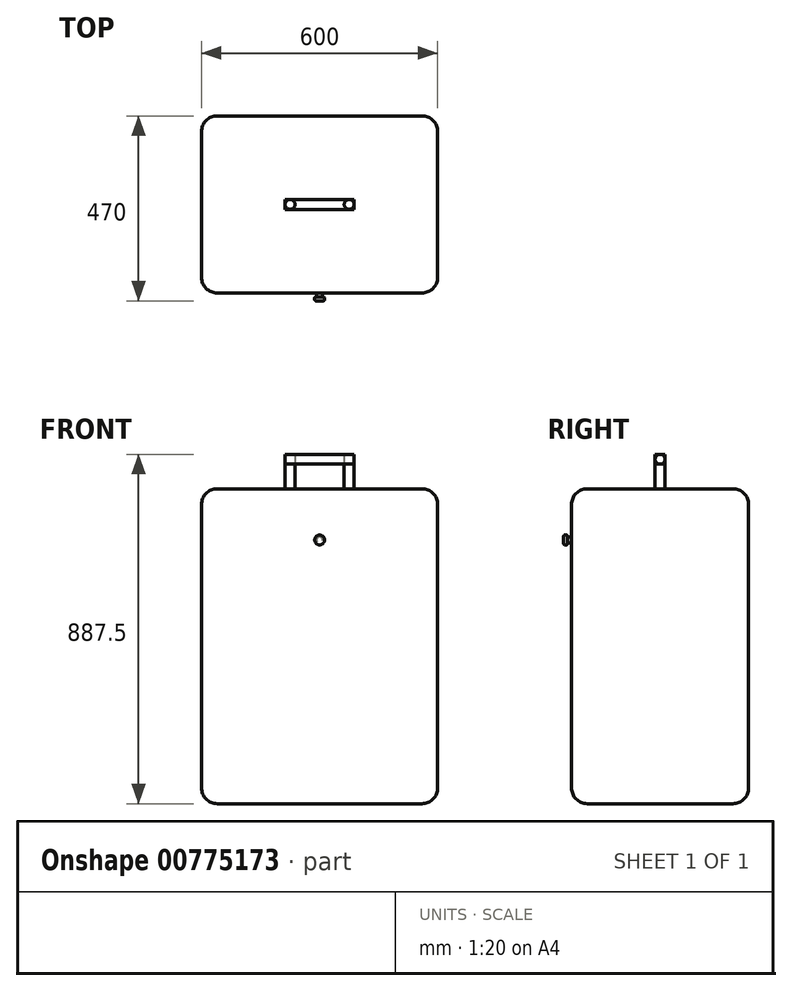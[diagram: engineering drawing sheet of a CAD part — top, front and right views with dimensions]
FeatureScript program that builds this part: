
annotation { "Feature Type Name" : "Feature", "Feature Type Description" : "" }
export const myFeature = defineFeature(function(context is Context, id is Id, definition is map)
    precondition{}
    {
        {
            var Q0;
            Q0=qCreatedBy(makeId("Top.planeOp"),FACE);
            var sketch = newSketch(context, id + "F0", { "sketchPlane" : qUnion([Q0])});
            skLineSegment(sketch, "E0.bottom", {"start": v(300, -225) * mm, "end": v(-300, -225) * mm});
            skLineSegment(sketch, "E0.top", {"start": v(300, 225) * mm, "end": v(-300, 225) * mm});
            skLineSegment(sketch, "E0.left", {"start": v(300, -225) * mm, "end": v(300, 225) * mm});
            skLineSegment(sketch, "E0.right", {"start": v(-300, -225) * mm, "end": v(-300, 225) * mm});
            skPoint(sketch, "E0.middle", {"position": v(0, 0) * mm});
            skSolve(sketch);
        }
        {
            var Q0;
            Q0 = qSketchRegion(id + "F0", true);
            extrude(context, id + "F1", {"entities" : qUnion([Q0]), "depth" : 800 * mm, "offsetDistance" : 25 * mm});
        }
        {
            var Q0;
            Q0=makeQuery(id+"F1.opExtrude","SWEPT_FACE",FACE,{"disambiguationData":[OSD([sQuery(id+"F0.wireOp",EDGE,"E0.bottom")])]});
            var Q1;
            Q1=makeQuery(id+"F1.opExtrude","CAP_FACE",FACE,{"disambiguationData":[OSD([sQuery(id+"F0.wireOp",EDGE,"E0.bottom"),sQuery(id+"F0.wireOp",EDGE,"E0.top"),sQuery(id+"F0.wireOp",EDGE,"E0.left"),sQuery(id+"F0.wireOp",EDGE,"E0.right")])],"isStart":false});
            var Q2;
            Q2=makeQuery(id+"F1.opExtrude","SWEPT_FACE",FACE,{"disambiguationData":[OSD([sQuery(id+"F0.wireOp",EDGE,"E0.top")])]});
            var Q3;
            Q3=makeQuery(id+"F1.opExtrude","CAP_FACE",FACE,{"disambiguationData":[OSD([sQuery(id+"F0.wireOp",EDGE,"E0.bottom"),sQuery(id+"F0.wireOp",EDGE,"E0.top"),sQuery(id+"F0.wireOp",EDGE,"E0.left"),sQuery(id+"F0.wireOp",EDGE,"E0.right")])],"isStart":true});
            fillet(context, id + "F2", {"entities" : qUnion([Q0, Q1, Q2, Q3]), "radius" : 40 * mm, "tangentPropagation" : true, "allowEdgeOverflow" : false});
        }
        {
            var Q0;
            Q0=makeQuery(id+"F1.opExtrude","CAP_FACE",FACE,{"disambiguationData":[OSD([sQuery(id+"F0.wireOp",EDGE,"E0.bottom"),sQuery(id+"F0.wireOp",EDGE,"E0.top"),sQuery(id+"F0.wireOp",EDGE,"E0.left"),sQuery(id+"F0.wireOp",EDGE,"E0.right")])],"isStart":false});
            var sketch = newSketch(context, id + "F3", { "sketchPlane" : qUnion([Q0])});
            skLineSegment(sketch, "E1", {"start": v(0, 185) * mm, "end": v(0, -185) * mm});
            skCircle(sketch, "E2", {"center": v(-75, 0) * mm, "radius": 12.5 * mm});
            skCircle(sketch, "E3.MirrorC", {"center": v(75, 0) * mm, "radius": 12.5 * mm});
            skSolve(sketch);
        }
        {
            var Q0;
            Q0 = qSketchRegion(id + "F3", true);
            extrude(context, id + "F4", {"entities" : qUnion([Q0]), "operationType" : NewBodyOperationType.ADD, "depth" : 75 * mm, "offsetDistance" : 25 * mm});
        }
        {
            var Q0;
            Q0=makeQuery(id+"F4.opExtrude","CAP_FACE",FACE,{"disambiguationData":[OSD([sQuery(id+"F3.wireOp",EDGE,"E2")])],"isStart":false});
            var sketch = newSketch(context, id + "F5", { "sketchPlane" : qUnion([Q0])});
            skLineSegment(sketch, "E4", {"start": v(-75, 0) * mm, "end": v(74.49, 0) * mm});
            skSolve(sketch);
        }
        {
            var Q0;
            Q0=qCreatedBy(makeId("Right.planeOp"),FACE);
            var sketch = newSketch(context, id + "F6", { "sketchPlane" : qUnion([Q0])});
            skCircle(sketch, "E5", {"center": v(0, 875) * mm, "radius": 12.5 * mm});
            skSolve(sketch);
        }
        {
            var Q0;
            Q0=makeQuery(id+"F5.imprint","IMPRINT",FACE,{"disambiguationData":[TD([[makeQuery(id+"F5.imprint","IMPRINT",EDGE,{"derivedFrom":makeQuery(id+"F4.opExtrude","CAP_EDGE",EDGE,{"disambiguationData":[OSD([sQuery(id+"F3.wireOp",EDGE,"E2")])],"isStart":false})}),1.0]])]});
            extrude(context, id + "F7", {"entities" : qUnion([Q0]), "operationType" : NewBodyOperationType.ADD, "oppositeDirection" : true, "depth" : 12.5 * mm, "offsetDistance" : 25 * mm});
        }
        {
            var Q0;
            Q0=makeQuery(id+"F4.opExtrude","CAP_FACE",FACE,{"disambiguationData":[OSD([sQuery(id+"F3.wireOp",EDGE,"E2")])],"isStart":false});
            extrude(context, id + "F8", {"entities" : qUnion([Q0]), "operationType" : NewBodyOperationType.ADD, "oppositeDirection" : true, "depth" : 12.5 * mm, "offsetDistance" : 25 * mm});
        }
        {
            var Q0;
            Q0=makeQuery(id+"F4.opExtrude","CAP_FACE",FACE,{"disambiguationData":[OSD([sQuery(id+"F3.wireOp",EDGE,"E2")])],"isStart":false});
            extrude(context, id + "F9", {"entities" : qUnion([Q0]), "operationType" : NewBodyOperationType.REMOVE, "oppositeDirection" : true, "depth" : 12.5 * mm, "offsetDistance" : 25 * mm});
        }
        {
            var Q0;
            Q0 = qSketchRegion(id + "F6", true);
            extrude(context, id + "F10", {"entities" : qUnion([Q0]), "oppositeDirection" : true, "depth" : 62.5 * mm, "offsetDistance" : 25 * mm});
        }
        {
            var Q0;
            Q0=makeQuery(id+"F10.opExtrude","CAP_FACE",FACE,{"disambiguationData":[OSD([sQuery(id+"F6.wireOp",EDGE,"E5")])],"isStart":true});
            extrude(context, id + "F11", {"entities" : qUnion([Q0]), "operationType" : NewBodyOperationType.ADD, "depth" : 62.5 * mm, "offsetDistance" : 25 * mm});
        }
        {
            var Q0;
            Q0=makeQuery(id+"F4.opExtrude","CAP_FACE",FACE,{"disambiguationData":[OSD([sQuery(id+"F3.wireOp",EDGE,"E3.MirrorC")])],"isStart":false});
            extrude(context, id + "F12", {"entities" : qUnion([Q0]), "operationType" : NewBodyOperationType.REMOVE, "oppositeDirection" : true, "depth" : 12.5 * mm, "offsetDistance" : 25 * mm});
        }
        {
            var Q0;
            Q0=makeQuery(id+"F11.opExtrude","CAP_FACE",FACE,{"disambiguationData":[OSD([sQuery(id+"F6.wireOp",EDGE,"E5")])],"isStart":false});
            extrude(context, id + "F13", {"entities" : qUnion([Q0]), "operationType" : NewBodyOperationType.ADD, "depth" : 25 * mm, "offsetDistance" : 25 * mm});
        }
        {
            var Q0;
            Q0=makeQuery(id+"F12.boolean.opBoolean","COPY",FACE,{"derivedFrom":makeQuery(id+"F12.opExtrude","CAP_FACE",FACE,{"disambiguationData":[OSD([sQuery(id+"F3.wireOp",EDGE,"E3.MirrorC")])],"isStart":false})});
            extrude(context, id + "F14", {"entities" : qUnion([Q0]), "depth" : 25 * mm, "offsetDistance" : 25 * mm});
        }
        {
            var Q0;
            Q0=makeQuery(id+"F10.opExtrude","CAP_FACE",FACE,{"disambiguationData":[OSD([sQuery(id+"F6.wireOp",EDGE,"E5")])],"isStart":false});
            extrude(context, id + "F15", {"entities" : qUnion([Q0]), "operationType" : NewBodyOperationType.ADD, "depth" : 25 * mm, "offsetDistance" : 25 * mm});
        }
        {
            var Q0;
            Q0=makeQuery(id+"F9.boolean.opBoolean","COPY",FACE,{"derivedFrom":makeQuery(id+"F9.opExtrude","CAP_FACE",FACE,{"disambiguationData":[OSD([sQuery(id+"F3.wireOp",EDGE,"E2")])],"isStart":false})});
            extrude(context, id + "F16", {"entities" : qUnion([Q0]), "depth" : 25 * mm, "offsetDistance" : 25 * mm});
        }
        {
            var Q0;
            Q0=makeQuery(id+"F1.opExtrude","SWEPT_FACE",FACE,{"disambiguationData":[OSD([sQuery(id+"F0.wireOp",EDGE,"E0.bottom")])]});
            var sketch = newSketch(context, id + "F17", { "sketchPlane" : qUnion([Q0])});
            skLineSegment(sketch, "E6.bottom", {"start": v(-260, 760) * mm, "end": v(260, 760) * mm});
            skLineSegment(sketch, "E6.top", {"start": v(-260, 580) * mm, "end": v(260, 580) * mm});
            skLineSegment(sketch, "E6.left", {"start": v(-260, 760) * mm, "end": v(-260, 580) * mm});
            skLineSegment(sketch, "E6.right", {"start": v(260, 760) * mm, "end": v(260, 580) * mm});
            skLineSegment(sketch, "E7.top", {"start": v(-260, 400) * mm, "end": v(260, 400) * mm});
            skLineSegment(sketch, "E7.left", {"start": v(-260, 580) * mm, "end": v(-260, 400) * mm});
            skLineSegment(sketch, "E7.right", {"start": v(260, 580) * mm, "end": v(260, 400) * mm});
            skLineSegment(sketch, "E8.top", {"start": v(-260, 220) * mm, "end": v(260, 220) * mm});
            skLineSegment(sketch, "E8.left", {"start": v(-260, 400) * mm, "end": v(-260, 220) * mm});
            skLineSegment(sketch, "E8.right", {"start": v(260, 400) * mm, "end": v(260, 220) * mm});
            skLineSegment(sketch, "E9.top", {"start": v(-260, 40) * mm, "end": v(260, 40) * mm});
            skLineSegment(sketch, "E9.left", {"start": v(-260, 220) * mm, "end": v(-260, 40) * mm});
            skLineSegment(sketch, "E9.right", {"start": v(260, 220) * mm, "end": v(260, 40) * mm});
            skLineSegment(sketch, "E10", {"start": v(0, 760) * mm, "end": v(0, 40) * mm, "construction": true});
            skLineSegment(sketch, "E11", {"start": v(-260, 670) * mm, "end": v(260, 670) * mm, "construction": true});
            skLineSegment(sketch, "E12", {"start": v(-260, 490) * mm, "end": v(260, 490) * mm, "construction": true});
            skLineSegment(sketch, "E13", {"start": v(-260, 310) * mm, "end": v(260, 310) * mm, "construction": true});
            skLineSegment(sketch, "E14", {"start": v(-260, 130) * mm, "end": v(260, 130) * mm, "construction": true});
            skSolve(sketch);
        }
        {
            var Q0;
            Q0=makeQuery(id+"F17.imprint","IMPRINT",FACE,{"disambiguationData":[TD([[makeQuery(id+"F17.imprint","IMPRINT",EDGE,{"derivedFrom":sQuery(id+"F17.wireOp",EDGE,"E6.bottom")}),1.0]])]});
            var sketch = newSketch(context, id + "F18", { "sketchPlane" : qUnion([Q0])});
            skCircle(sketch, "E15", {"center": v(0, 670) * mm, "radius": 7.5 * mm});
            skSolve(sketch);
        }
        {
            var Q0;
            Q0=makeQuery(id+"F18.imprint","IMPRINT",FACE,{"disambiguationData":[TD([[makeQuery(id+"F18.imprint","IMPRINT",EDGE,{"derivedFrom":sQuery(id+"F18.wireOp",EDGE,"E15")}),1.0]])]});
            extrude(context, id + "F19", {"entities" : qUnion([Q0]), "operationType" : NewBodyOperationType.ADD, "depth" : 10 * mm, "offsetDistance" : 25 * mm});
        }
        {
            var Q0;
            Q0=makeQuery(id+"F19.opExtrude","CAP_FACE",FACE,{"disambiguationData":[OSD([sQuery(id+"F18.wireOp",EDGE,"E15")])],"isStart":false});
            var sketch = newSketch(context, id + "F20", { "sketchPlane" : qUnion([Q0])});
            skCircle(sketch, "E16", {"center": v(0, 670) * mm, "radius": 12.5 * mm});
            skSolve(sketch);
        }
        {
            var Q0;
            Q0=makeQuery(id+"F20.imprint","IMPRINT",FACE,{"disambiguationData":[TD([[makeQuery(id+"F20.imprint","IMPRINT",EDGE,{"derivedFrom":sQuery(id+"F20.wireOp",EDGE,"E16")}),1.0]])]});
            var Q1;
            Q1=makeQuery(id+"F20.imprint","IMPRINT",FACE,{"disambiguationData":[TD([[makeQuery(id+"F20.imprint","IMPRINT",EDGE,{"derivedFrom":makeQuery(id+"F19.opExtrude","CAP_EDGE",EDGE,{"disambiguationData":[OSD([sQuery(id+"F18.wireOp",EDGE,"E15")])],"isStart":false})}),1.0]])]});
            extrude(context, id + "F21", {"entities" : qUnion([Q0, Q1]), "operationType" : NewBodyOperationType.ADD, "depth" : 10 * mm, "offsetDistance" : 25 * mm});
        }
        {
            var Q0;
            Q0=makeQuery(id+"F21.opExtrude","CAP_FACE",FACE,{"disambiguationData":[OSD([sQuery(id+"F20.wireOp",EDGE,"E16")])],"isStart":false});
            fillet(context, id + "F22", {"entities" : qUnion([Q0]), "radius" : 3 * mm, "tangentPropagation" : true, "allowEdgeOverflow" : false});
        }
        {
            var Q0;
            Q0=makeQuery(id+"F21.opExtrude","CAP_EDGE",EDGE,{"disambiguationData":[OSD([sQuery(id+"F20.wireOp",EDGE,"E16")])],"isStart":true});
            fillet(context, id + "F23", {"entities" : qUnion([Q0]), "radius" : 3 * mm, "tangentPropagation" : true, "allowEdgeOverflow" : false});
        }
    });
